# Revit family: IO Controler MS660404M
name_source: partatom
category: Datengeräte
units: mm (PartAtom-declared; Revit-internal decimal feet)

## family parameters
Arbeitsebenenbasiert = Nein
Beim Laden mit Abzugskörper schneiden = Nein
Bemaßung runder Anschluss = Durchmesser verwenden
Beschriftungsausrichtung beibehalten = Nein
Gemeinsam genutzt = Nein
Immer vertikal = Ja
OmniClass-Nummer = 23.85.50.17
OmniClass-Titel = Communication and Data Processing Equipment
Raumberechnungspunkt = Nein
Teiletyp = Normal

## types (1)
- I/O Controler MS660404M
    Anschluss 1 = 10x I/O Input
    Anschluss 2 = 4x I/O Output
    Anschluss 3 = 2x 24VDC Ausgang
    Anschluss 4 = 1x 24VDC Eingang
    Anschluss 5 = 1x 10/100TX RJ-45 PoE+ PD
    Artikelnummer = MS660404M
    Beschreibung = Smart I/O Controller Digital / Analog
    Hersteller = MICROSENS
    Material = Metallverkleidung
    Material 2 = Kunststoff
    Vorgabe-Ansicht = 0 mm  [stored 0 ft]

note: [stored X ft] marks values corroborated as IEEE doubles in the binary element streams (Revit-internal decimal feet)
